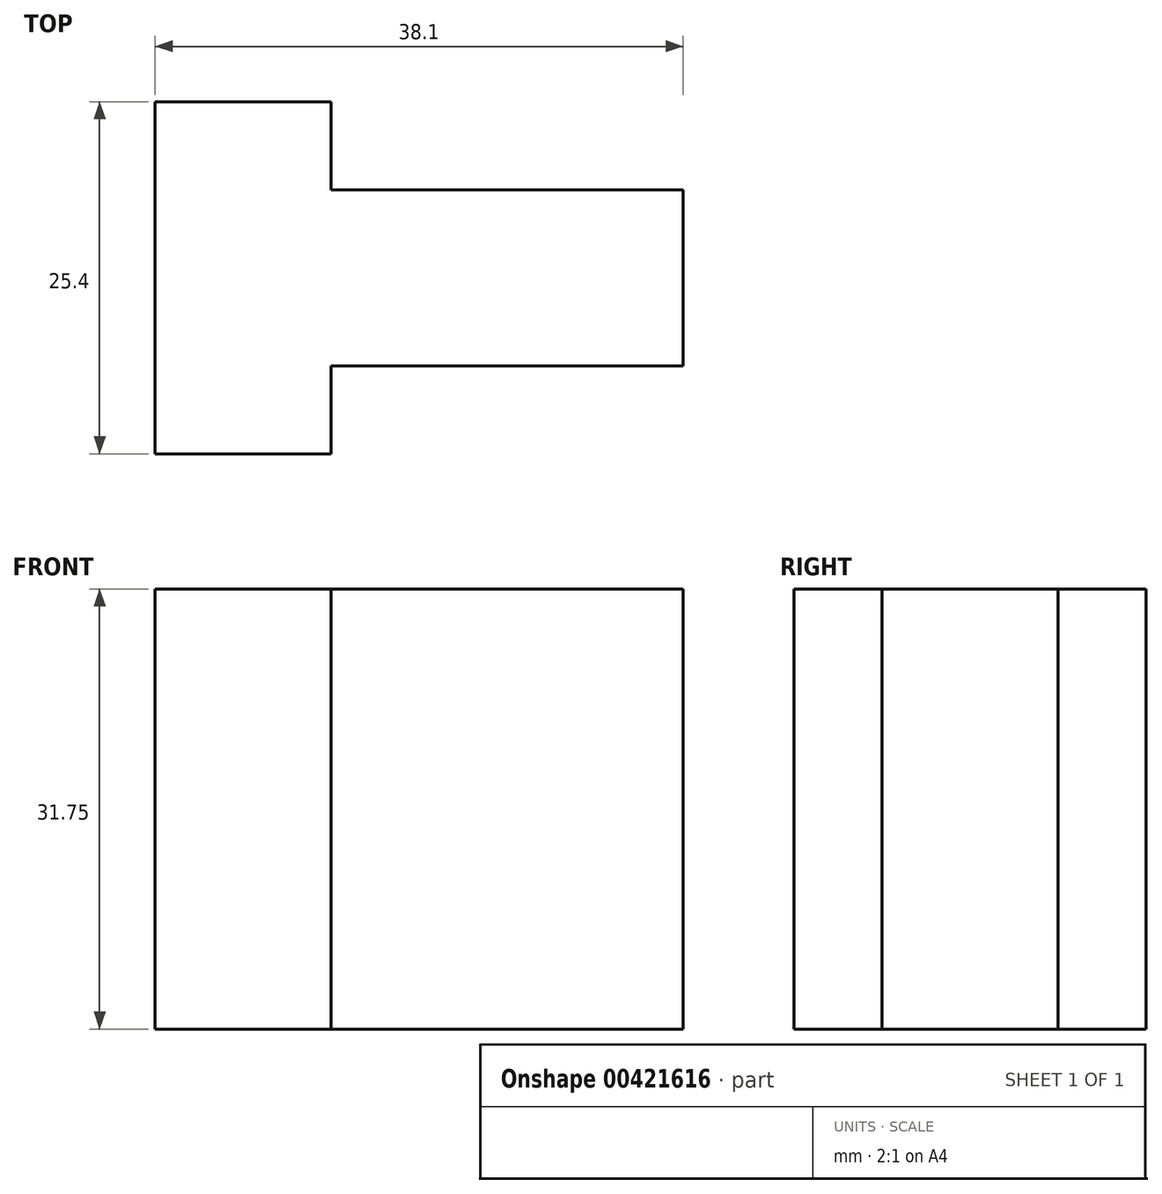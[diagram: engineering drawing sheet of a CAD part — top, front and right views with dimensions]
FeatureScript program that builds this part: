
annotation { "Feature Type Name" : "Feature", "Feature Type Description" : "" }
export const myFeature = defineFeature(function(context is Context, id is Id, definition is map)
    precondition{}
    {
        {
            var Q0;
            Q0=qCreatedBy(makeId("Top.planeOp"),FACE);
            var sketch = newSketch(context, id + "F0", { "sketchPlane" : qUnion([Q0])});
            skLineSegment(sketch, "E0", {"start": v(0, 0) * mm, "end": v(0, 25.4) * mm});
            skLineSegment(sketch, "E1", {"start": v(0, 25.4) * mm, "end": v(12.7, 25.4) * mm});
            skLineSegment(sketch, "E2", {"start": v(12.7, 25.4) * mm, "end": v(12.7, 19.05) * mm});
            skLineSegment(sketch, "E3", {"start": v(0, 0) * mm, "end": v(12.7, 0) * mm});
            skPoint(sketch, "E3.endSnap0", {"position": v(12.7, 22.23) * mm});
            skLineSegment(sketch, "E4", {"start": v(12.7, 0) * mm, "end": v(12.7, 6.35) * mm});
            skLineSegment(sketch, "E5", {"start": v(12.7, 19.05) * mm, "end": v(38.1, 19.05) * mm});
            skLineSegment(sketch, "E6", {"start": v(12.7, 6.35) * mm, "end": v(38.1, 6.35) * mm});
            skLineSegment(sketch, "E7", {"start": v(38.1, 19.05) * mm, "end": v(38.1, 6.35) * mm});
            skSolve(sketch);
        }
        {
            var Q0;
            Q0=makeQuery(id+"F0.imprint","IMPRINT",FACE,{"disambiguationData":[TD([[makeQuery(id+"F0.imprint","IMPRINT",EDGE,{"derivedFrom":sQuery(id+"F0.wireOp",EDGE,"E0")}),-1.0]])]});
            extrude(context, id + "F1", {"entities" : qUnion([Q0]), "depth" : 31.75 * mm});
        }
    });
